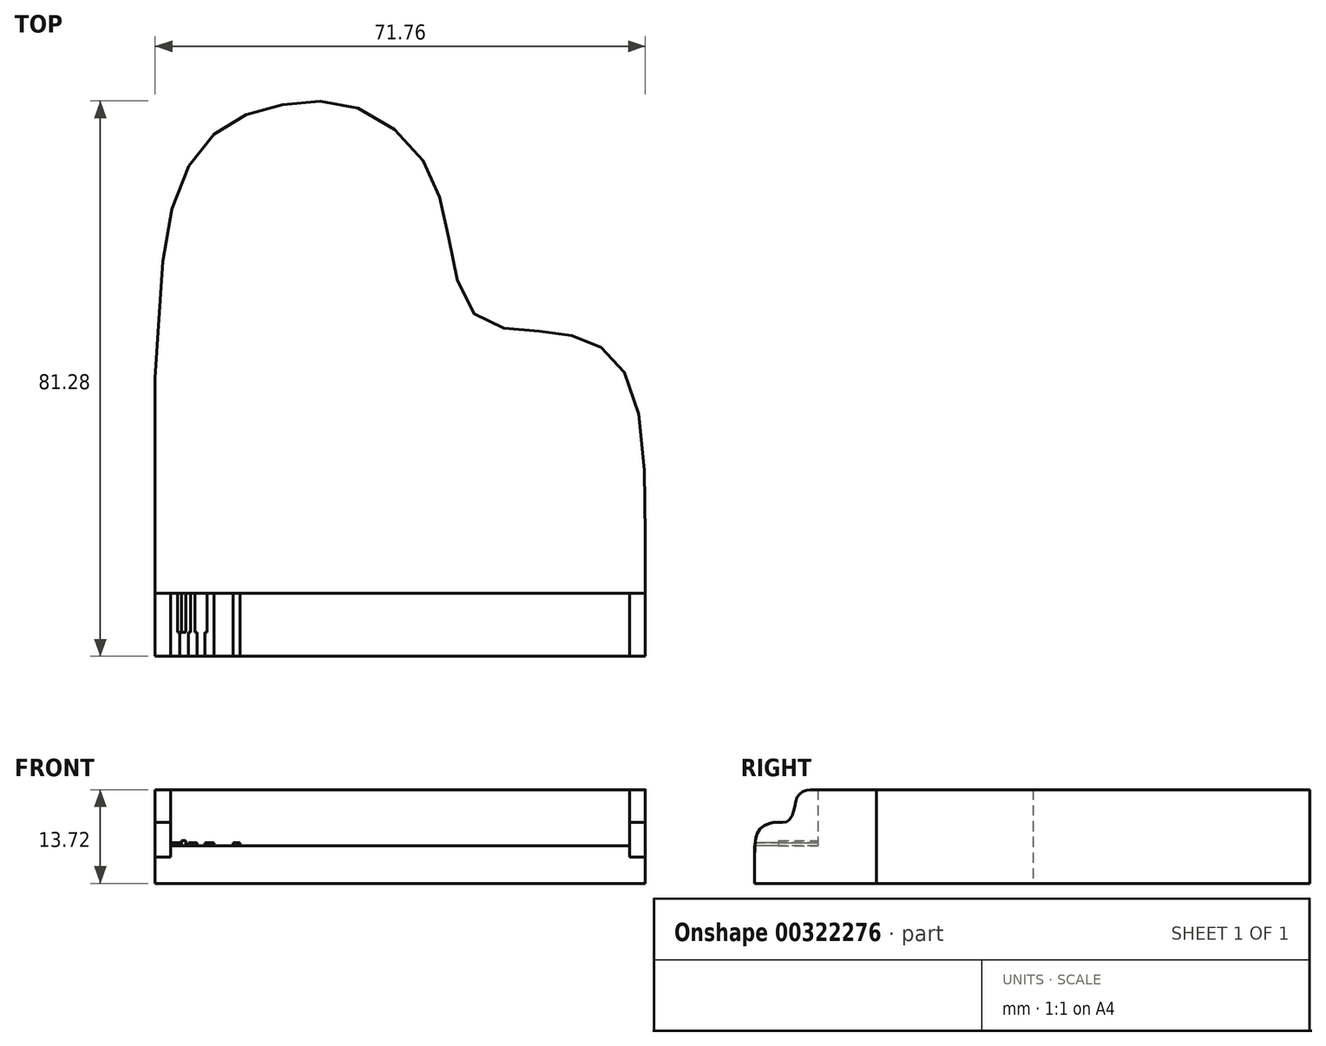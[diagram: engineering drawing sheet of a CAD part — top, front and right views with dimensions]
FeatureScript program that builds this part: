
annotation { "Feature Type Name" : "Feature", "Feature Type Description" : "" }
export const myFeature = defineFeature(function(context is Context, id is Id, definition is map)
    precondition{}
    {
        {
            var Q0;
            Q0=qCreatedBy(makeId("Top.planeOp"),FACE);
            var sketch = newSketch(context, id + "F0", { "sketchPlane" : qUnion([Q0])});
            skLineSegment(sketch, "E0", {"start": v(-71.94, 0) * mm, "end": v(-71.94, 31.48) * mm});
            skLineSegment(sketch, "E1", {"start": v(-0.2, 0) * mm, "end": v(-0.2, 8.55) * mm});
            skPoint(sketch, "E2", {"position": v(35.87, -2.74) * mm});
            skFitSpline(sketch, "E3", {"points": [v(-71.94, 31.48) * mm, v(-69.66, 55.46) * mm, v(-63, 67.46) * mm, v(-53.4, 71.45) * mm, v(-42.75, 71.19) * mm, v(-32.62, 63.2) * mm, v(-28.89, 51.46) * mm, v(-24.89, 40.54) * mm, v(-16.63, 38.4) * mm, v(-8.9, 37.07) * mm, v(-2.77, 31.48) * mm, v(-0.2, 8.55) * mm], "startDerivative": vector(15.72, 194.83) * mm, "endDerivative": vector(-2.3, -224.94) * mm});
            skLineSegment(sketch, "E4", {"start": v(0, 0) * mm, "end": v(-71.94, 0) * mm});
            skSolve(sketch);
        }
        {
            var Q0;
            Q0 = qSketchRegion(id + "F0", true);
            extrude(context, id + "F1", {"entities" : qUnion([Q0]), "depth" : 13.72 * mm});
        }
        {
            var Q0;
            Q0=makeQuery(id+"F1.opExtrude","SWEPT_FACE",FACE,{"disambiguationData":[OSD([sQuery(id+"F0.wireOp",EDGE,"E1")])]});
            var sketch = newSketch(context, id + "F2", { "sketchPlane" : qUnion([Q0])});
            skPoint(sketch, "E5", {"position": v(0, 13.72) * mm});
            skLineSegment(sketch, "E6", {"start": v(0, 0) * mm, "end": v(-9.25, 0) * mm});
            skLineSegment(sketch, "E7", {"start": v(-9.25, 0) * mm, "end": v(-9.25, 3.84) * mm});
            skFitSpline(sketch, "E8", {"points": [v(-9.25, 3.84) * mm, v(-8.87, 7.35) * mm, v(-8, 8.35) * mm, v(-7.12, 8.77) * mm, v(-6.24, 8.93) * mm, v(-5.36, 8.93) * mm, v(-4.44, 9.06) * mm, v(-3.73, 10.02) * mm, v(-3.4, 11.23) * mm, v(-3.06, 12.53) * mm, v(-2.52, 13.24) * mm, v(-1.69, 13.65) * mm, v(-0.85, 13.7) * mm, v(0, 13.72) * mm], "startDerivative": vector(0.39, 30.18) * mm, "endDerivative": vector(12.94, 0.56) * mm});
            skLineSegment(sketch, "E9", {"start": v(0, 13.72) * mm, "end": v(0, 0) * mm});
            skSolve(sketch);
        }
        {
            var Q0;
            Q0 = qSketchRegion(id + "F2", true);
            extrude(context, id + "F3", {"entities" : qUnion([Q0]), "operationType" : NewBodyOperationType.ADD, "oppositeDirection" : true, "depth" : 2.3 * mm});
        }
        {
            var Q0;
            Q0=makeQuery(id+"F1.opExtrude","SWEPT_FACE",FACE,{"disambiguationData":[OSD([sQuery(id+"F0.wireOp",EDGE,"E4")])]});
            var sketch = newSketch(context, id + "F4", { "sketchPlane" : qUnion([Q0])});
            skLineSegment(sketch, "E10", {"start": v(-69.65, 0) * mm, "end": v(-69.65, 5.49) * mm});
            skLineSegment(sketch, "E11", {"start": v(-69.65, 5.49) * mm, "end": v(-2.48, 5.49) * mm});
            skLineSegment(sketch, "E12", {"start": v(-2.48, 5.49) * mm, "end": v(-2.48, 0) * mm});
            skSolve(sketch);
        }
        {
            var Q0;
            {var subQ0=sQuery(id+"F4.wireOp",EDGE,"E10");Q0=makeQuery(id+"F4.imprint","IMPRINT",FACE,{"disambiguationData":[TD([[makeQuery(id+"F4.imprint","IMPRINT",EDGE,{"derivedFrom":subQ0}),-1.0]])]});}
            extrude(context, id + "F5", {"entities" : qUnion([Q0]), "operationType" : NewBodyOperationType.ADD, "depth" : 9.25 * mm});
        }
        {
            var Q0;
            Q0=makeQuery(id+"F5.opExtrude","SWEPT_FACE",FACE,{"disambiguationData":[OSD([sQuery(id+"F4.wireOp",EDGE,"E10")])]});
            var sketch = newSketch(context, id + "F6", { "sketchPlane" : qUnion([Q0])});
            skLineSegment(sketch, "E13", {"start": v(0, 13.72) * mm, "end": v(0, 0) * mm});
            skLineSegment(sketch, "E14.MirrorCS", {"start": v(0, 0) * mm, "end": v(9.25, 0) * mm});
            skLineSegment(sketch, "E15.MirrorCS", {"start": v(9.25, 0) * mm, "end": v(9.25, 3.84) * mm});
            skFitSpline(sketch, "E16.MirrorCS", {"points": [v(9.25, 3.84) * mm, v(8.87, 7.35) * mm, v(8, 8.35) * mm, v(7.12, 8.77) * mm, v(6.24, 8.93) * mm, v(5.36, 8.93) * mm, v(4.44, 9.06) * mm, v(3.73, 10.02) * mm, v(3.4, 11.23) * mm, v(3.06, 12.53) * mm, v(2.52, 13.24) * mm, v(1.69, 13.65) * mm, v(0.85, 13.7) * mm, v(0, 13.72) * mm], "startDerivative": vector(-0.39, 30.18) * mm, "endDerivative": vector(-12.94, 0.56) * mm});
            skSolve(sketch);
        }
        {
            var Q0;
            Q0 = qSketchRegion(id + "F6", true);
            extrude(context, id + "F7", {"entities" : qUnion([Q0]), "operationType" : NewBodyOperationType.ADD, "depth" : 2.3 * mm});
        }
        {
            var Q0;
            Q0=makeQuery(id+"F5.opExtrude","SWEPT_FACE",FACE,{"disambiguationData":[OSD([sQuery(id+"F4.wireOp",EDGE,"E11")])]});
            var sketch = newSketch(context, id + "F8", { "sketchPlane" : qUnion([Q0])});
            skLineSegment(sketch, "E17.top", {"start": v(-69.65, -9.2) * mm, "end": v(-68.36, -9.2) * mm});
            skLineSegment(sketch, "E17.left", {"start": v(-69.65, 0.05) * mm, "end": v(-69.65, -9.2) * mm});
            skLineSegment(sketch, "E18.left", {"start": v(-68.36, -5.75) * mm, "end": v(-68.36, -9.2) * mm});
            skLineSegment(sketch, "E19", {"start": v(-68.68, -5.75) * mm, "end": v(-68.36, -5.75) * mm});
            skLineSegment(sketch, "E20", {"start": v(-68.68, -5.75) * mm, "end": v(-68.68, 0.05) * mm});
            skLineSegment(sketch, "E21", {"start": v(-69.65, 0.05) * mm, "end": v(-68.68, 0.05) * mm});
            skLineSegment(sketch, "E22.top", {"start": v(-67.07, -9.2) * mm, "end": v(-65.78, -9.2) * mm});
            skLineSegment(sketch, "E22.left", {"start": v(-67.07, -5.75) * mm, "end": v(-67.07, -9.2) * mm});
            skLineSegment(sketch, "E22.right", {"start": v(-65.78, -5.75) * mm, "end": v(-65.78, -9.2) * mm});
            skLineSegment(sketch, "E23.MirrorCS", {"start": v(-66.75, -5.75) * mm, "end": v(-67.07, -5.75) * mm});
            skLineSegment(sketch, "E24", {"start": v(-66.75, -5.75) * mm, "end": v(-66.75, 0.05) * mm});
            skLineSegment(sketch, "E25.MirrorCS", {"start": v(-65.78, -5.75) * mm, "end": v(-66.1, -5.75) * mm});
            skLineSegment(sketch, "E26", {"start": v(-66.1, -5.75) * mm, "end": v(-66.1, 0.05) * mm});
            skLineSegment(sketch, "E27", {"start": v(-66.75, 0.05) * mm, "end": v(-66.1, 0.05) * mm});
            skLineSegment(sketch, "E28.top", {"start": v(-64.63, -9.2) * mm, "end": v(-63.34, -9.2) * mm});
            skLineSegment(sketch, "E28.right", {"start": v(-63.34, 0.05) * mm, "end": v(-63.34, -9.2) * mm});
            skLineSegment(sketch, "E29.right", {"start": v(-64.63, -5.75) * mm, "end": v(-64.63, -9.2) * mm});
            skLineSegment(sketch, "E30", {"start": v(-64.63, -5.75) * mm, "end": v(-64.32, -5.75) * mm});
            skLineSegment(sketch, "E31", {"start": v(-64.32, -5.75) * mm, "end": v(-64.32, 0.05) * mm});
            skLineSegment(sketch, "E32", {"start": v(-64.32, 0.05) * mm, "end": v(-63.34, 0.05) * mm});
            skLineSegment(sketch, "E33", {"start": v(-68.08, -5.75) * mm, "end": v(-68.08, 0.05) * mm});
            skLineSegment(sketch, "E34", {"start": v(-67.45, -5.75) * mm, "end": v(-67.45, 0.05) * mm});
            skLineSegment(sketch, "E35", {"start": v(-68.08, 0.05) * mm, "end": v(-67.45, 0.05) * mm});
            skLineSegment(sketch, "E36", {"start": v(-68.08, -5.75) * mm, "end": v(-67.45, -5.75) * mm});
            skLineSegment(sketch, "E37.right", {"start": v(-59.51, 0.05) * mm, "end": v(-59.51, -9.2) * mm});
            skLineSegment(sketch, "E38", {"start": v(-59.51, 0.05) * mm, "end": v(-60.53, 0) * mm});
            skLineSegment(sketch, "E39", {"start": v(-59.51, -9.2) * mm, "end": v(-60.53, -9.2) * mm});
            skLineSegment(sketch, "E40", {"start": v(-60.53, -9.2) * mm, "end": v(-60.53, 0) * mm});
            skSolve(sketch);
        }
        {
            var Q0;
            {var subQ7=sQuery(id+"F8.wireOp",EDGE,"E17.top");Q0=makeQuery(id+"F8.imprint","IMPRINT",FACE,{"disambiguationData":[TD([[makeQuery(id+"F8.imprint","IMPRINT",EDGE,{"derivedFrom":subQ7}),1.0]])]});}
            var Q1;
            Q1=makeQuery(id+"F8.imprint","IMPRINT",FACE,{"disambiguationData":[TD([[makeQuery(id+"F8.imprint","IMPRINT",EDGE,{"derivedFrom":sQuery(id+"F8.wireOp",EDGE,"E22.top")}),1.0]])]});
            var Q2;
            {var subQ2=sQuery(id+"F8.wireOp",EDGE,"E28.top");Q2=makeQuery(id+"F8.imprint","IMPRINT",FACE,{"disambiguationData":[TD([[makeQuery(id+"F8.imprint","IMPRINT",EDGE,{"derivedFrom":subQ2}),1.0]])]});}
            extrude(context, id + "F9", {"entities" : qUnion([Q0, Q1, Q2]), "depth" : 0.46 * mm});
        }
        {
            var Q0;
            {var subQ0=sQuery(id+"F8.wireOp",EDGE,"E36");Q0=makeQuery(id+"F8.imprint","IMPRINT",FACE,{"disambiguationData":[TD([[makeQuery(id+"F8.imprint","IMPRINT",EDGE,{"derivedFrom":subQ0}),1.0]])]});}
            extrude(context, id + "F10", {"entities" : qUnion([Q0]), "depth" : 0.76 * mm});
        }
        {
            var Q0;
            {var subQ0=sQuery(id+"F8.wireOp",EDGE,"E39");Q0=makeQuery(id+"F8.imprint","IMPRINT",FACE,{"disambiguationData":[TD([[makeQuery(id+"F8.imprint","IMPRINT",EDGE,{"derivedFrom":subQ0}),-1.0]])]});}
            extrude(context, id + "F11", {"entities" : qUnion([Q0]), "depth" : 0.46 * mm});
        }
        {
            var Q0;
            Q0=qCreatedBy(makeId("Front.planeOp"),FACE);
            var sketch = newSketch(context, id + "F12", { "sketchPlane" : qUnion([Q0])});
            skLineSegment(sketch, "E41", {"start": v(-50.8, 0) * mm, "end": v(-48.24, 0) * mm});
            skLineSegment(sketch, "E42", {"start": v(-48.24, 0) * mm, "end": v(-48.24, -26.22) * mm, "construction": true});
            skLineSegment(sketch, "E43", {"start": v(-50.8, 0) * mm, "end": v(-50.8, -1.05) * mm});
            skArc(sketch, "E44", {"start": v(-50.8, -1.05) * mm, "mid": v(-52.34, -2.72) * mm, "end": v(-50.8, -4.4) * mm});
            skLineSegment(sketch, "E45", {"start": v(-50.8, -4.4) * mm, "end": v(-50.8, -5.55) * mm});
            skArc(sketch, "E46", {"start": v(-50.8, -8.42) * mm, "mid": v(-49.45, -6.99) * mm, "end": v(-50.8, -5.55) * mm});
            skLineSegment(sketch, "E47", {"start": v(-50.8, -8.42) * mm, "end": v(-50.8, -9.26) * mm});
            skArc(sketch, "E48", {"start": v(-50.8, -9.26) * mm, "mid": v(-51.92, -10.16) * mm, "end": v(-50.8, -11.06) * mm});
            skLineSegment(sketch, "E49", {"start": v(-50.8, -11.06) * mm, "end": v(-50.8, -11.71) * mm});
            skPoint(sketch, "E50", {"position": v(-50.8, -11.71) * mm});
            skFitSpline(sketch, "E51", {"points": [v(-50.8, -11.71) * mm, v(-52.66, -11.95) * mm, v(-53.43, -12.34) * mm, v(-52.69, -12.72) * mm, v(-50.8, -12.94) * mm], "startDerivative": vector(-6.44, -0.47) * mm, "endDerivative": vector(6.54, -0.37) * mm});
            skLineSegment(sketch, "E52", {"start": v(-50.8, -12.94) * mm, "end": v(-49.5, -24.24) * mm});
            skArc(sketch, "E53", {"start": v(-49.5, -24.24) * mm, "mid": v(-50.36, -24.8) * mm, "end": v(-49.5, -25.37) * mm});
            skLineSegment(sketch, "E54", {"start": v(-49.5, -25.37) * mm, "end": v(-49.15, -26.22) * mm});
            skLineSegment(sketch, "E55", {"start": v(-49.15, -26.22) * mm, "end": v(-48.24, -26.22) * mm});
            skSolve(sketch);
        }
        {
            var Q0;
            Q0 = qConstructionFilter(qBodyType(qCreatedBy(id + "F12" ,EDGE), BodyType.WIRE), ConstructionObject.NO);
            var Q1;
            Q1=sQuery(id+"F12.wireOp",EDGE,"E42");
            revolve(context, id + "F13", {"bodyType" : ToolBodyType.SURFACE, "surfaceEntities" : qUnion([Q0]), "axis" : qUnion([Q1]), "revolveType" : RevolveType.FULL});
        }
    });
